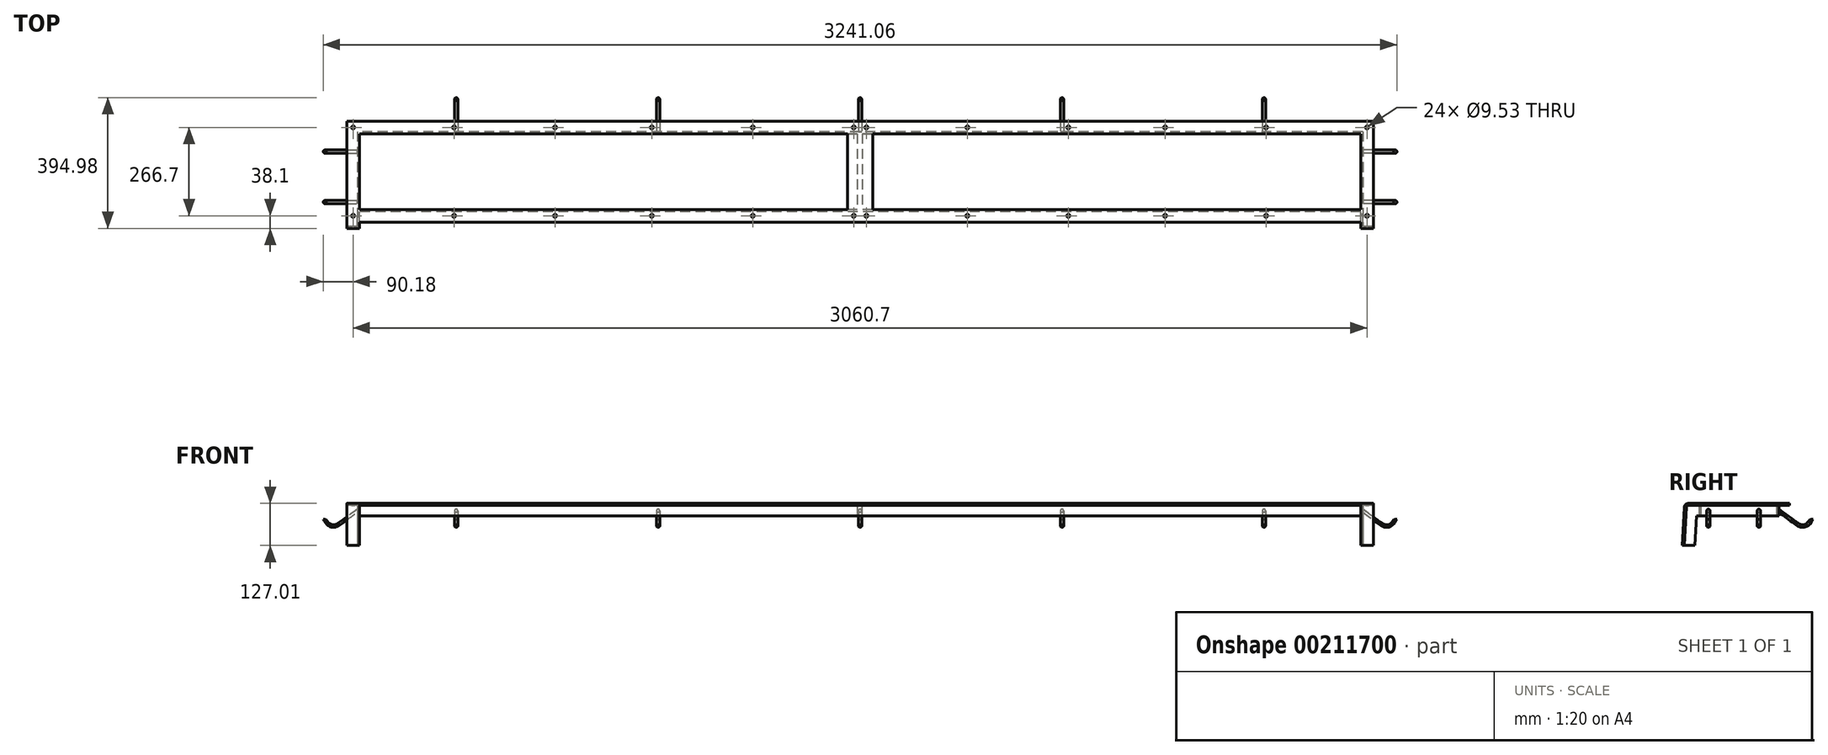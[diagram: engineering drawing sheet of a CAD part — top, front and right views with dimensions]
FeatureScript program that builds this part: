
annotation { "Feature Type Name" : "Feature", "Feature Type Description" : "" }
export const myFeature = defineFeature(function(context is Context, id is Id, definition is map)
    precondition{}
    {
        {
            var Q0;
            Q0=qCreatedBy(makeId("Right.planeOp"),FACE);
            var sketch = newSketch(context, id + "F0", { "sketchPlane" : qUnion([Q0])});
            skLineSegment(sketch, "E0", {"start": v(304.8, 0) * mm, "end": v(0, 0) * mm, "construction": true});
            skArc(sketch, "E1", {"start": v(0, 0) * mm, "mid": v(-6.55, -2.6) * mm, "end": v(-9.51, -9) * mm, "construction": true});
            skLineSegment(sketch, "E2", {"start": v(-9.51, -9) * mm, "end": v(-15.87, -123.83) * mm, "construction": true});
            skLineSegment(sketch, "E3.0", {"start": v(-12.68, -8.82) * mm, "end": v(-19.05, -123.83) * mm});
            skArc(sketch, "E3.1", {"start": v(0, 3.18) * mm, "mid": v(-8.73, -0.3) * mm, "end": v(-12.68, -8.82) * mm});
            skLineSegment(sketch, "E3.2", {"start": v(304.8, 3.18) * mm, "end": v(0, 3.18) * mm});
            skLineSegment(sketch, "E4", {"start": v(-15.87, -123.83) * mm, "end": v(-19.05, -123.83) * mm});
            skLineSegment(sketch, "E5", {"start": v(304.8, 3.18) * mm, "end": v(304.8, 0) * mm});
            skLineSegment(sketch, "E6.0", {"start": v(-6.34, -9.17) * mm, "end": v(-12.7, -123.83) * mm});
            skArc(sketch, "E6.1", {"start": v(0, -3.17) * mm, "mid": v(-4.36, -4.91) * mm, "end": v(-6.34, -9.17) * mm});
            skLineSegment(sketch, "E6.2", {"start": v(304.8, -3.17) * mm, "end": v(0, -3.17) * mm});
            skLineSegment(sketch, "E7", {"start": v(-15.87, -123.83) * mm, "end": v(-12.7, -123.83) * mm});
            skLineSegment(sketch, "E8", {"start": v(304.8, -3.17) * mm, "end": v(304.8, 0) * mm});
            skLineSegment(sketch, "E9", {"start": v(273.05, 0) * mm, "end": v(273.05, -34.92) * mm});
            skLineSegment(sketch, "E10", {"start": v(-12.7, -123.83) * mm, "end": v(19.1, -123.83) * mm});
            skLineSegment(sketch, "E11.0", {"start": v(24.03, -34.92) * mm, "end": v(19.1, -123.83) * mm});
            skLineSegment(sketch, "E11.1", {"start": v(273.05, -34.92) * mm, "end": v(24.03, -34.92) * mm});
            skSolve(sketch);
        }
        {
            var Q0;
            Q0=makeQuery(id+"F0.imprint","IMPRINT",FACE,{"disambiguationData":[TD([[makeQuery(id+"F0.imprint","IMPRINT",EDGE,{"derivedFrom":sQuery(id+"F0.wireOp",EDGE,"E3.0")}),1.0]])]});
            extrude(context, id + "F1", {"entities" : qUnion([Q0]), "depth" : 1549.4 * mm, "hasSecondDirection" : true, "secondDirectionOppositeDirection" : true, "secondDirectionDepth" : 1549.4 * mm});
        }
        {
            var Q0;
            Q0=makeQuery(id+"F0.imprint","IMPRINT",FACE,{"disambiguationData":[TD([[makeQuery(id+"F0.imprint","IMPRINT",EDGE,{"derivedFrom":sQuery(id+"F0.wireOp",EDGE,"E6.0")}),1.0]])]});
            extrude(context, id + "F2", {"entities" : qUnion([Q0]), "operationType" : NewBodyOperationType.ADD, "depth" : 1517.65 * mm, "hasSecondDirection" : true, "secondDirectionOppositeDirection" : true, "secondDirectionDepth" : 1517.65 * mm});
        }
        {
            var Q0;
            Q0=makeQuery(id+"F1.opExtrude","SWEPT_FACE",FACE,{"disambiguationData":[OSD([sQuery(id+"F0.wireOp",EDGE,"E3.2")])]});
            var sketch = newSketch(context, id + "F3", { "sketchPlane" : qUnion([Q0])});
            skLineSegment(sketch, "E12.bottom", {"start": v(1511.3, 266.7) * mm, "end": v(-1511.3, 266.7) * mm});
            skLineSegment(sketch, "E12.top", {"start": v(1511.3, -266.7) * mm, "end": v(-1511.3, -266.7) * mm});
            skLineSegment(sketch, "E12.left", {"start": v(1511.3, 266.7) * mm, "end": v(1511.3, -266.7) * mm});
            skLineSegment(sketch, "E12.right", {"start": v(-1511.3, 266.7) * mm, "end": v(-1511.3, -266.7) * mm});
            skPoint(sketch, "E12.middle", {"position": v(0, 0) * mm});
            skSolve(sketch);
        }
        {
            var Q0;
            Q0 = qSketchRegion(id + "F3", true);
            extrude(context, id + "F4", {"entities" : qUnion([Q0]), "operationType" : NewBodyOperationType.REMOVE, "endBound" : BoundingType.THROUGH_ALL, "oppositeDirection" : true, "depth" : 25.4 * mm});
        }
        {
            var Q0;
            Q0=qCreatedBy(makeId("Right.planeOp"),FACE);
            var sketch = newSketch(context, id + "F5", { "sketchPlane" : qUnion([Q0])});
            skLineSegment(sketch, "E13.0", {"start": v(304.8, 3.18) * mm, "end": v(0, 3.18) * mm, "construction": true});
            skPoint(sketch, "E14.0", {"position": v(266.7, 3.18) * mm});
            skLineSegment(sketch, "E15", {"start": v(0, 3.18) * mm, "end": v(38.1, 3.18) * mm});
            skLineSegment(sketch, "E16.0", {"start": v(273.05, -34.92) * mm, "end": v(24.03, -34.92) * mm, "construction": true});
            skLineSegment(sketch, "E17", {"start": v(38.1, 3.18) * mm, "end": v(38.1, -34.92) * mm});
            skLineSegment(sketch, "E18", {"start": v(38.1, -34.93) * mm, "end": v(31.75, -34.93) * mm});
            skLineSegment(sketch, "E19", {"start": v(31.75, -34.92) * mm, "end": v(31.75, -3.17) * mm});
            skLineSegment(sketch, "E20", {"start": v(31.75, -3.17) * mm, "end": v(0, -3.17) * mm});
            skLineSegment(sketch, "E21", {"start": v(0, 3.18) * mm, "end": v(0, -3.17) * mm});
            skPoint(sketch, "E22.0", {"position": v(0, 3.18) * mm});
            skSolve(sketch);
        }
        {
            var Q0;
            Q0=makeQuery(id+"F5.imprint","IMPRINT",FACE,{"disambiguationData":[TD([[makeQuery(id+"F5.imprint","IMPRINT",EDGE,{"derivedFrom":sQuery(id+"F5.wireOp",EDGE,"E15")}),-1.0]])]});
            var Q1;
            Q1=makeQuery(id+"F1.opExtrude","SWEPT_BODY",BODY,{"disambiguationData":[OSD([sQuery(id+"F0.wireOp",EDGE,"E3.0"),sQuery(id+"F0.wireOp",EDGE,"E3.1"),sQuery(id+"F0.wireOp",EDGE,"E3.2"),sQuery(id+"F0.wireOp",EDGE,"E4"),sQuery(id+"F0.wireOp",EDGE,"E5"),sQuery(id+"F0.wireOp",EDGE,"E6.0"),sQuery(id+"F0.wireOp",EDGE,"E6.1"),sQuery(id+"F0.wireOp",EDGE,"E6.2"),sQuery(id+"F0.wireOp",EDGE,"E7"),sQuery(id+"F0.wireOp",EDGE,"E8")])]});
            var Q2;
            Q2=makeQuery(id+"F1.opExtrude","SWEPT_BODY",BODY,{"disambiguationData":[OSD([sQuery(id+"F0.wireOp",EDGE,"E3.0"),sQuery(id+"F0.wireOp",EDGE,"E3.1"),sQuery(id+"F0.wireOp",EDGE,"E3.2"),sQuery(id+"F0.wireOp",EDGE,"E4"),sQuery(id+"F0.wireOp",EDGE,"E5"),sQuery(id+"F0.wireOp",EDGE,"E6.0"),sQuery(id+"F0.wireOp",EDGE,"E6.1"),sQuery(id+"F0.wireOp",EDGE,"E6.2"),sQuery(id+"F0.wireOp",EDGE,"E7"),sQuery(id+"F0.wireOp",EDGE,"E8")])]});
            extrude(context, id + "F6", {"entities" : qUnion([Q0]), "operationType" : NewBodyOperationType.ADD, "endBound" : BoundingType.UP_TO_BODY, "endBoundEntityBody" : qUnion([Q1]), "depth" : 25.4 * mm, "hasSecondDirection" : true, "secondDirectionBound" : SecondDirectionBoundingType.UP_TO_BODY, "secondDirectionOppositeDirection" : true, "secondDirectionBoundEntityBody" : qUnion([Q2]), "secondDirectionDepth" : 25.4 * mm});
        }
        {
            var Q0;
            Q0=qCreatedBy(makeId("Right.planeOp"),FACE);
            var sketch = newSketch(context, id + "F7", { "sketchPlane" : qUnion([Q0])});
            skPoint(sketch, "E23.0", {"position": v(38.1, 3.18) * mm});
            skLineSegment(sketch, "E24", {"start": v(266.7, 0) * mm, "end": v(38.1, 0) * mm, "construction": true});
            skLineSegment(sketch, "E25.2", {"start": v(266.7, 3.18) * mm, "end": v(38.1, 3.18) * mm});
            skLineSegment(sketch, "E26", {"start": v(266.7, 3.18) * mm, "end": v(266.7, 0) * mm});
            skLineSegment(sketch, "E27.2", {"start": v(266.7, -3.17) * mm, "end": v(38.1, -3.17) * mm});
            skLineSegment(sketch, "E28", {"start": v(266.7, -3.17) * mm, "end": v(266.7, 0) * mm});
            skLineSegment(sketch, "E29", {"start": v(266.7, 0) * mm, "end": v(266.7, -34.92) * mm});
            skLineSegment(sketch, "E30.1", {"start": v(266.7, -34.92) * mm, "end": v(38.1, -34.92) * mm});
            skPoint(sketch, "E31.0", {"position": v(266.7, 3.18) * mm});
            skPoint(sketch, "E32.0", {"position": v(38.1, -34.92) * mm});
            skLineSegment(sketch, "E33", {"start": v(38.1, -34.92) * mm, "end": v(38.1, 3.18) * mm});
            skSolve(sketch);
        }
        {
            var Q0;
            {var subQ3=sQuery(id+"F7.wireOp",EDGE,"E25.2");Q0=makeQuery(id+"F7.imprint","IMPRINT",FACE,{"disambiguationData":[TD([[makeQuery(id+"F7.imprint","IMPRINT",EDGE,{"derivedFrom":subQ3}),1.0]])]});}
            extrude(context, id + "F8", {"entities" : qUnion([Q0]), "operationType" : NewBodyOperationType.ADD, "depth" : 38.1 * mm, "hasSecondDirection" : true, "secondDirectionOppositeDirection" : true, "secondDirectionDepth" : 38.1 * mm});
        }
        {
            var Q0;
            {var subQ0=sQuery(id+"F7.wireOp",EDGE,"E27.2");Q0=makeQuery(id+"F7.imprint","IMPRINT",FACE,{"disambiguationData":[TD([[makeQuery(id+"F7.imprint","IMPRINT",EDGE,{"derivedFrom":subQ0}),1.0]])]});}
            extrude(context, id + "F9", {"entities" : qUnion([Q0]), "operationType" : NewBodyOperationType.ADD, "depth" : 6.35 * mm, "hasSecondDirection" : true, "secondDirectionOppositeDirection" : true, "secondDirectionDepth" : 8.9 * mm});
        }
        {
            var Q0;
            Q0=makeQuery(id+"F8.boolean.opBoolean","MERGE",FACE,{"derivedFrom":[makeQuery(id+"F6.boolean.opBoolean","MERGE",FACE,{"derivedFrom":[makeQuery(id+"F1.opExtrude","SWEPT_FACE",FACE,{"disambiguationData":[OSD([sQuery(id+"F0.wireOp",EDGE,"E3.2")])]}),makeQuery(id+"F6.opExtrude","SWEPT_FACE",FACE,{"disambiguationData":[OSD([sQuery(id+"F5.wireOp",EDGE,"E15")])]})]}),makeQuery(id+"F8.opExtrude","SWEPT_FACE",FACE,{"disambiguationData":[OSD([sQuery(id+"F7.wireOp",EDGE,"E25.2")])]})]});
            var sketch = newSketch(context, id + "F10", { "sketchPlane" : qUnion([Q0])});
            skPoint(sketch, "E34", {"position": v(-1530.35, 285.75) * mm});
            skPoint(sketch, "E35", {"position": v(-19.05, 285.75) * mm});
            skPoint(sketch, "E36", {"position": v(-628.65, 285.75) * mm});
            skPoint(sketch, "E37", {"position": v(-920.75, 285.75) * mm});
            skPoint(sketch, "E38", {"position": v(-1225.55, 285.75) * mm});
            skPoint(sketch, "E39", {"position": v(-323.85, 285.75) * mm});
            skLineSegment(sketch, "E40", {"start": v(-1319.31, 152.4) * mm, "end": v(-616.3, 152.4) * mm, "construction": true});
            skPoint(sketch, "E41.MirrorP", {"position": v(-19.05, 19.05) * mm});
            skPoint(sketch, "E42.MirrorP", {"position": v(-323.85, 19.05) * mm});
            skPoint(sketch, "E43.MirrorP", {"position": v(-628.65, 19.05) * mm});
            skPoint(sketch, "E44.MirrorP", {"position": v(-920.75, 19.05) * mm});
            skPoint(sketch, "E45.MirrorP", {"position": v(-1225.55, 19.05) * mm});
            skPoint(sketch, "E46.MirrorP", {"position": v(-1530.35, 19.05) * mm});
            skPoint(sketch, "E47.MirrorP", {"position": v(1530.35, 285.75) * mm});
            skPoint(sketch, "E48.MirrorP", {"position": v(1530.35, 19.05) * mm});
            skPoint(sketch, "E49.MirrorP", {"position": v(1225.55, 19.05) * mm});
            skPoint(sketch, "E50.MirrorP", {"position": v(1225.55, 285.75) * mm});
            skPoint(sketch, "E51.MirrorP", {"position": v(920.75, 285.75) * mm});
            skPoint(sketch, "E52.MirrorP", {"position": v(920.75, 19.05) * mm});
            skPoint(sketch, "E53.MirrorP", {"position": v(628.65, 285.75) * mm});
            skPoint(sketch, "E54.MirrorP", {"position": v(628.65, 19.05) * mm});
            skPoint(sketch, "E55.MirrorP", {"position": v(323.85, 285.75) * mm});
            skPoint(sketch, "E56.MirrorP", {"position": v(323.85, 19.05) * mm});
            skPoint(sketch, "E57.MirrorP", {"position": v(19.05, 19.05) * mm});
            skPoint(sketch, "E58.MirrorP", {"position": v(19.05, 285.75) * mm});
            skSolve(sketch);
        }
        {
            var Q0;
            Q0=sQuery(id+"F10.wireOp",VERTEX,"E48.MirrorP");
            var Q1;
            Q1=sQuery(id+"F10.wireOp",VERTEX,"E47.MirrorP");
            var Q2;
            Q2=sQuery(id+"F10.wireOp",VERTEX,"E50.MirrorP");
            var Q3;
            Q3=sQuery(id+"F10.wireOp",VERTEX,"E49.MirrorP");
            var Q4;
            Q4=sQuery(id+"F10.wireOp",VERTEX,"E51.MirrorP");
            var Q5;
            Q5=sQuery(id+"F10.wireOp",VERTEX,"E53.MirrorP");
            var Q6;
            Q6=sQuery(id+"F10.wireOp",VERTEX,"E52.MirrorP");
            var Q7;
            Q7=sQuery(id+"F10.wireOp",VERTEX,"E54.MirrorP");
            var Q8;
            Q8=sQuery(id+"F10.wireOp",VERTEX,"E56.MirrorP");
            var Q9;
            Q9=sQuery(id+"F10.wireOp",VERTEX,"E55.MirrorP");
            var Q10;
            Q10=sQuery(id+"F10.wireOp",VERTEX,"E35");
            var Q11;
            Q11=sQuery(id+"F10.wireOp",VERTEX,"E57.MirrorP");
            var Q12;
            Q12=sQuery(id+"F10.wireOp",VERTEX,"E58.MirrorP");
            var Q13;
            Q13=sQuery(id+"F10.wireOp",VERTEX,"E41.MirrorP");
            var Q14;
            Q14=sQuery(id+"F10.wireOp",VERTEX,"E42.MirrorP");
            var Q15;
            Q15=sQuery(id+"F10.wireOp",VERTEX,"E39");
            var Q16;
            Q16=sQuery(id+"F10.wireOp",VERTEX,"E36");
            var Q17;
            Q17=sQuery(id+"F10.wireOp",VERTEX,"E43.MirrorP");
            var Q18;
            Q18=sQuery(id+"F10.wireOp",VERTEX,"E44.MirrorP");
            var Q19;
            Q19=sQuery(id+"F10.wireOp",VERTEX,"E37");
            var Q20;
            Q20=sQuery(id+"F10.wireOp",VERTEX,"E38");
            var Q21;
            Q21=sQuery(id+"F10.wireOp",VERTEX,"E45.MirrorP");
            var Q22;
            Q22=sQuery(id+"F10.wireOp",VERTEX,"E34");
            var Q23;
            Q23=sQuery(id+"F10.wireOp",VERTEX,"E46.MirrorP");
            var Q24;
            Q24=makeQuery(id+"F1.opExtrude","SWEPT_BODY",BODY,{"disambiguationData":[OSD([sQuery(id+"F0.wireOp",EDGE,"E3.0"),sQuery(id+"F0.wireOp",EDGE,"E3.1"),sQuery(id+"F0.wireOp",EDGE,"E3.2"),sQuery(id+"F0.wireOp",EDGE,"E4"),sQuery(id+"F0.wireOp",EDGE,"E5"),sQuery(id+"F0.wireOp",EDGE,"E6.0"),sQuery(id+"F0.wireOp",EDGE,"E6.1"),sQuery(id+"F0.wireOp",EDGE,"E6.2"),sQuery(id+"F0.wireOp",EDGE,"E7"),sQuery(id+"F0.wireOp",EDGE,"E8")])]});
            hole(context, id + "F11", {"style" : HoleStyle.SIMPLE, "endStyle" : HoleEndStyle.BLIND, "holeDiameter" : 9.52 * mm, "holeDepth" : 12.7 * mm, "startFromSketch" : true, "locations" : qUnion([Q0, Q1, Q2, Q3, Q4, Q5, Q6, Q7, Q8, Q9, Q10, Q11, Q12, Q13, Q14, Q15, Q16, Q17, Q18, Q19, Q20, Q21, Q22, Q23]), "scope" : qUnion([Q24])});
        }
        {
            var Q0;
            Q0=qCreatedBy(makeId("Right.planeOp"),FACE);
            var sketch = newSketch(context, id + "F12", { "sketchPlane" : qUnion([Q0])});
            skPoint(sketch, "E59.0", {"position": v(273.05, -19.05) * mm});
            skFitSpline(sketch, "E60", {"points": [v(273.05, -19.05) * mm, v(342.92, -65.18) * mm, v(371.2, -45.3) * mm], "startDerivative": vector(281.31, -205.32) * mm, "endDerivative": vector(85.1, 152.4) * mm});
            skSolve(sketch);
        }
        {
            var Q0;
            Q0=makeQuery(id+"F2.opExtrude","SWEPT_FACE",FACE,{"disambiguationData":[OSD([sQuery(id+"F0.wireOp",EDGE,"E9")])]});
            var sketch = newSketch(context, id + "F13", { "sketchPlane" : qUnion([Q0])});
            skPoint(sketch, "E61.0", {"position": v(0, -19.05) * mm});
            skCircle(sketch, "E62", {"center": v(0, -19.05) * mm, "radius": 4.76 * mm});
            skSolve(sketch);
        }
        {
            var Q0;
            Q0 = qSketchRegion(id + "F13", true);
            var Q1;
            Q1 = qConstructionFilter(qBodyType(qCreatedBy(id + "F12" ,EDGE), BodyType.WIRE), ConstructionObject.NO);
            sweep(context, id + "F14", {"operationType" : NewBodyOperationType.ADD, "profiles" : qUnion([Q0]), "path" : qUnion([Q1])});
        }
        {
            var Q0;
            Q0=makeQuery(id+"F2.opExtrude","SWEPT_FACE",FACE,{"disambiguationData":[OSD([sQuery(id+"F0.wireOp",EDGE,"E9")])]});
            var sketch = newSketch(context, id + "F15", { "sketchPlane" : qUnion([Q0])});
            skPoint(sketch, "E63", {"position": v(0, -19.05) * mm});
            skPoint(sketch, "E64", {"position": v(609.6, -19.05) * mm});
            skPoint(sketch, "E65", {"position": v(-609.6, -19.05) * mm});
            skPoint(sketch, "E66", {"position": v(1219.2, -19.05) * mm});
            skPoint(sketch, "E67", {"position": v(-1219.2, -19.05) * mm});
            skSolve(sketch);
        }
        {
            var Q0;
            Q0=qCreatedBy(makeId("Right.planeOp"),FACE);
            cPlane(context, id + "F16", {"entities" : qUnion([Q0]), "cplaneType" : CPlaneType.OFFSET, "offset" : 1219.2 * mm, "width" : 152.4 * mm, "height" : 152.4 * mm});
        }
        {
            var Q0;
            Q0=qCreatedBy(makeId("Right.planeOp"),FACE);
            cPlane(context, id + "F17", {"entities" : qUnion([Q0]), "cplaneType" : CPlaneType.OFFSET, "offset" : 609.6 * mm, "width" : 152.4 * mm, "height" : 152.4 * mm});
        }
        {
            var Q0;
            Q0=qCreatedBy(makeId("Right.planeOp"),FACE);
            cPlane(context, id + "F18", {"entities" : qUnion([Q0]), "cplaneType" : CPlaneType.OFFSET, "offset" : 609.6 * mm, "oppositeDirection" : true, "width" : 152.4 * mm, "height" : 152.4 * mm});
        }
        {
            var Q0;
            Q0=qCreatedBy(makeId("Right.planeOp"),FACE);
            cPlane(context, id + "F19", {"entities" : qUnion([Q0]), "cplaneType" : CPlaneType.OFFSET, "offset" : 1219.2 * mm, "oppositeDirection" : true, "width" : 152.4 * mm, "height" : 152.4 * mm});
        }
        {
            var Q0;
            Q0=qCreatedBy(id+"F16.planeOp",FACE);
            var sketch = newSketch(context, id + "F20", { "sketchPlane" : qUnion([Q0])});
            skPoint(sketch, "E68.0", {"position": v(273.05, -19.05) * mm});
            skFitSpline(sketch, "E69", {"points": [v(273.05, -19.05) * mm, v(342.92, -65.18) * mm, v(371.2, -45.3) * mm], "startDerivative": vector(281.31, -205.32) * mm, "endDerivative": vector(85.1, 152.4) * mm});
            skSolve(sketch);
        }
        {
            var Q0;
            Q0=qCreatedBy(id+"F17.planeOp",FACE);
            var sketch = newSketch(context, id + "F21", { "sketchPlane" : qUnion([Q0])});
            skPoint(sketch, "E70.0", {"position": v(273.05, -19.05) * mm});
            skFitSpline(sketch, "E71", {"points": [v(273.05, -19.05) * mm, v(342.92, -65.18) * mm, v(371.2, -45.3) * mm], "startDerivative": vector(281.31, -205.32) * mm, "endDerivative": vector(85.1, 152.4) * mm});
            skSolve(sketch);
        }
        {
            var Q0;
            Q0=qCreatedBy(id+"F18.planeOp",FACE);
            var sketch = newSketch(context, id + "F22", { "sketchPlane" : qUnion([Q0])});
            skPoint(sketch, "E72.0", {"position": v(273.05, -19.05) * mm});
            skFitSpline(sketch, "E73", {"points": [v(273.05, -19.05) * mm, v(342.92, -65.18) * mm, v(371.2, -45.3) * mm], "startDerivative": vector(281.31, -205.32) * mm, "endDerivative": vector(85.1, 152.4) * mm});
            skSolve(sketch);
        }
        {
            var Q0;
            Q0=qCreatedBy(id+"F19.planeOp",FACE);
            var sketch = newSketch(context, id + "F23", { "sketchPlane" : qUnion([Q0])});
            skPoint(sketch, "E74.0", {"position": v(273.05, -19.05) * mm});
            skFitSpline(sketch, "E75", {"points": [v(273.05, -19.05) * mm, v(342.92, -65.18) * mm, v(371.2, -45.3) * mm], "startDerivative": vector(281.31, -205.32) * mm, "endDerivative": vector(85.1, 152.4) * mm});
            skSolve(sketch);
        }
        {
            var Q0;
            {var subQ0=sQuery(id+"F0.wireOp",EDGE,"E9");Q0=makeQuery(id+"F15.imprint","IMPRINT",FACE,{"disambiguationData":[TD([[makeQuery(id+"F15.imprint","IMPRINT",EDGE,{"derivedFrom":makeQuery(id+"F2.opExtrude","CAP_EDGE",EDGE,{"disambiguationData":[OSD([subQ0])],"isStart":true})}),-1.0]])]});}
            var sketch = newSketch(context, id + "F24", { "sketchPlane" : qUnion([Q0])});
            skPoint(sketch, "E76.0", {"position": v(-1219.2, -19.05) * mm});
            skCircle(sketch, "E77", {"center": v(-1219.2, -19.05) * mm, "radius": 4.76 * mm});
            skSolve(sketch);
        }
        {
            var Q0;
            {var subQ0=sQuery(id+"F0.wireOp",EDGE,"E9");Q0=makeQuery(id+"F15.imprint","IMPRINT",FACE,{"disambiguationData":[TD([[makeQuery(id+"F15.imprint","IMPRINT",EDGE,{"derivedFrom":makeQuery(id+"F2.opExtrude","CAP_EDGE",EDGE,{"disambiguationData":[OSD([subQ0])],"isStart":true})}),-1.0]])]});}
            var sketch = newSketch(context, id + "F25", { "sketchPlane" : qUnion([Q0])});
            skPoint(sketch, "E78.0", {"position": v(-609.6, -19.05) * mm});
            skCircle(sketch, "E79", {"center": v(-609.6, -19.05) * mm, "radius": 4.76 * mm});
            skSolve(sketch);
        }
        {
            var Q0;
            {var subQ0=sQuery(id+"F0.wireOp",EDGE,"E9");Q0=makeQuery(id+"F15.imprint","IMPRINT",FACE,{"disambiguationData":[TD([[makeQuery(id+"F15.imprint","IMPRINT",EDGE,{"derivedFrom":makeQuery(id+"F2.opExtrude","CAP_EDGE",EDGE,{"disambiguationData":[OSD([subQ0])],"isStart":true})}),-1.0]])]});}
            var sketch = newSketch(context, id + "F26", { "sketchPlane" : qUnion([Q0])});
            skPoint(sketch, "E80.0", {"position": v(609.6, -19.05) * mm});
            skCircle(sketch, "E81", {"center": v(609.6, -19.05) * mm, "radius": 4.76 * mm});
            skSolve(sketch);
        }
        {
            var Q0;
            {var subQ0=sQuery(id+"F0.wireOp",EDGE,"E9");Q0=makeQuery(id+"F15.imprint","IMPRINT",FACE,{"disambiguationData":[TD([[makeQuery(id+"F15.imprint","IMPRINT",EDGE,{"derivedFrom":makeQuery(id+"F2.opExtrude","CAP_EDGE",EDGE,{"disambiguationData":[OSD([subQ0])],"isStart":true})}),-1.0]])]});}
            var sketch = newSketch(context, id + "F27", { "sketchPlane" : qUnion([Q0])});
            skPoint(sketch, "E82.0", {"position": v(1219.2, -19.05) * mm});
            skCircle(sketch, "E83", {"center": v(1219.2, -19.05) * mm, "radius": 4.76 * mm});
            skSolve(sketch);
        }
        {
            var Q0;
            Q0 = qSketchRegion(id + "F24", true);
            var Q1;
            Q1 = qConstructionFilter(qBodyType(qCreatedBy(id + "F20" ,EDGE), BodyType.WIRE), ConstructionObject.NO);
            sweep(context, id + "F28", {"operationType" : NewBodyOperationType.ADD, "profiles" : qUnion([Q0]), "path" : qUnion([Q1])});
        }
        {
            var Q0;
            Q0 = qSketchRegion(id + "F25", true);
            var Q1;
            Q1 = qConstructionFilter(qBodyType(qCreatedBy(id + "F21" ,EDGE), BodyType.WIRE), ConstructionObject.NO);
            sweep(context, id + "F29", {"operationType" : NewBodyOperationType.ADD, "profiles" : qUnion([Q0]), "path" : qUnion([Q1])});
        }
        {
            var Q0;
            Q0 = qSketchRegion(id + "F26", true);
            var Q1;
            Q1 = qConstructionFilter(qBodyType(qCreatedBy(id + "F22" ,EDGE), BodyType.WIRE), ConstructionObject.NO);
            sweep(context, id + "F30", {"operationType" : NewBodyOperationType.ADD, "profiles" : qUnion([Q0]), "path" : qUnion([Q1])});
        }
        {
            var Q0;
            Q0 = qSketchRegion(id + "F27", true);
            var Q1;
            Q1 = qConstructionFilter(qBodyType(qCreatedBy(id + "F23" ,EDGE), BodyType.WIRE), ConstructionObject.NO);
            sweep(context, id + "F31", {"operationType" : NewBodyOperationType.ADD, "profiles" : qUnion([Q0]), "path" : qUnion([Q1])});
        }
        {
            var Q0;
            Q0=makeQuery(id+"F2.opExtrude","CAP_FACE",FACE,{"disambiguationData":[OSD([sQuery(id+"F0.wireOp",EDGE,"E6.0"),sQuery(id+"F0.wireOp",EDGE,"E6.1"),sQuery(id+"F0.wireOp",EDGE,"E6.2"),sQuery(id+"F0.wireOp",EDGE,"E9"),sQuery(id+"F0.wireOp",EDGE,"E10"),sQuery(id+"F0.wireOp",EDGE,"E11.0"),sQuery(id+"F0.wireOp",EDGE,"E11.1")])],"isStart":false});
            var sketch = newSketch(context, id + "F32", { "sketchPlane" : qUnion([Q0])});
            skPoint(sketch, "E84", {"position": v(212.72, -19.05) * mm});
            skPoint(sketch, "E84.positionSnap0", {"position": v(273.05, -19.05) * mm});
            skPoint(sketch, "E85", {"position": v(60.32, -19.05) * mm});
            skSolve(sketch);
        }
        {
            var Q0;
            Q0=makeQuery(id+"F32.imprint","IMPRINT",FACE,{"disambiguationData":[TD([[makeQuery(id+"F32.imprint","IMPRINT",EDGE,{"derivedFrom":makeQuery(id+"F2.opExtrude","CAP_EDGE",EDGE,{"disambiguationData":[OSD([sQuery(id+"F0.wireOp",EDGE,"E9")])],"isStart":false})}),-1.0]])]});
            var sketch = newSketch(context, id + "F33", { "sketchPlane" : qUnion([Q0])});
            skPoint(sketch, "E86.0", {"position": v(60.32, -19.05) * mm});
            skCircle(sketch, "E87", {"center": v(60.32, -19.05) * mm, "radius": 4.76 * mm});
            skSolve(sketch);
        }
        {
            var Q0;
            Q0=makeQuery(id+"F32.imprint","IMPRINT",FACE,{"disambiguationData":[TD([[makeQuery(id+"F32.imprint","IMPRINT",EDGE,{"derivedFrom":makeQuery(id+"F2.opExtrude","CAP_EDGE",EDGE,{"disambiguationData":[OSD([sQuery(id+"F0.wireOp",EDGE,"E9")])],"isStart":false})}),-1.0]])]});
            var sketch = newSketch(context, id + "F34", { "sketchPlane" : qUnion([Q0])});
            skPoint(sketch, "E88.0", {"position": v(212.72, -19.05) * mm});
            skCircle(sketch, "E89", {"center": v(212.72, -19.05) * mm, "radius": 4.76 * mm});
            skSolve(sketch);
        }
        {
            var Q0;
            Q0=makeQuery(id+"F2.opExtrude","CAP_FACE",FACE,{"disambiguationData":[OSD([sQuery(id+"F0.wireOp",EDGE,"E6.0"),sQuery(id+"F0.wireOp",EDGE,"E6.1"),sQuery(id+"F0.wireOp",EDGE,"E6.2"),sQuery(id+"F0.wireOp",EDGE,"E9"),sQuery(id+"F0.wireOp",EDGE,"E10"),sQuery(id+"F0.wireOp",EDGE,"E11.0"),sQuery(id+"F0.wireOp",EDGE,"E11.1")])],"isStart":true});
            var sketch = newSketch(context, id + "F35", { "sketchPlane" : qUnion([Q0])});
            skPoint(sketch, "E90.0", {"position": v(-212.72, -19.05) * mm});
            skPoint(sketch, "E91.0", {"position": v(-60.32, -19.05) * mm});
            skCircle(sketch, "E92", {"center": v(-212.72, -19.05) * mm, "radius": 4.76 * mm});
            skSolve(sketch);
        }
        {
            var Q0;
            Q0=makeQuery(id+"F35.imprint","IMPRINT",FACE,{"disambiguationData":[TD([[makeQuery(id+"F35.imprint","IMPRINT",EDGE,{"derivedFrom":sQuery(id+"F35.wireOp",EDGE,"E92")}),-1.0]])]});
            var sketch = newSketch(context, id + "F36", { "sketchPlane" : qUnion([Q0])});
            skPoint(sketch, "E93.0", {"position": v(-60.32, -19.05) * mm});
            skCircle(sketch, "E94", {"center": v(-60.32, -19.05) * mm, "radius": 4.76 * mm});
            skSolve(sketch);
        }
        {
            var Q0;
            Q0=qCreatedBy(makeId("Front.planeOp"),FACE);
            cPlane(context, id + "F37", {"entities" : qUnion([Q0]), "cplaneType" : CPlaneType.OFFSET, "offset" : 60.32 * mm, "oppositeDirection" : true, "width" : 152.4 * mm, "height" : 152.4 * mm});
        }
        {
            var Q0;
            Q0=qCreatedBy(makeId("Front.planeOp"),FACE);
            cPlane(context, id + "F38", {"entities" : qUnion([Q0]), "cplaneType" : CPlaneType.OFFSET, "offset" : 212.72 * mm, "oppositeDirection" : true, "width" : 152.4 * mm, "height" : 152.4 * mm});
        }
        {
            var Q0;
            Q0=qCreatedBy(id+"F37.planeOp",FACE);
            var sketch = newSketch(context, id + "F39", { "sketchPlane" : qUnion([Q0])});
            skPoint(sketch, "E95.0", {"position": v(1517.65, -19.05) * mm});
            skFitSpline(sketch, "E96", {"points": [v(1517.65, -19.05) * mm, v(1587.52, -65.18) * mm, v(1615.8, -45.3) * mm], "startDerivative": vector(281.31, -205.32) * mm, "endDerivative": vector(85.1, 152.4) * mm});
            skSolve(sketch);
        }
        {
            var Q0;
            Q0=qCreatedBy(id+"F38.planeOp",FACE);
            var sketch = newSketch(context, id + "F40", { "sketchPlane" : qUnion([Q0])});
            skPoint(sketch, "E97.0", {"position": v(1517.65, -19.05) * mm});
            skFitSpline(sketch, "E98", {"points": [v(1517.65, -19.05) * mm, v(1587.52, -65.18) * mm, v(1615.8, -45.3) * mm], "startDerivative": vector(281.31, -205.32) * mm, "endDerivative": vector(85.1, 152.4) * mm});
            skSolve(sketch);
        }
        {
            var Q0;
            Q0=qCreatedBy(id+"F37.planeOp",FACE);
            var sketch = newSketch(context, id + "F41", { "sketchPlane" : qUnion([Q0])});
            skPoint(sketch, "E99.0", {"position": v(-1517.65, -19.05) * mm});
            skFitSpline(sketch, "E100.MirrorCS", {"points": [v(-1517.65, -19.05) * mm, v(-1587.52, -65.18) * mm, v(-1615.8, -45.3) * mm], "startDerivative": vector(-281.31, -205.32) * mm, "endDerivative": vector(-85.1, 152.4) * mm});
            skSolve(sketch);
        }
        {
            var Q0;
            Q0=qCreatedBy(id+"F38.planeOp",FACE);
            var sketch = newSketch(context, id + "F42", { "sketchPlane" : qUnion([Q0])});
            skPoint(sketch, "E101.0", {"position": v(-1517.65, -19.05) * mm});
            skFitSpline(sketch, "E102.MirrorCS", {"points": [v(-1517.65, -19.05) * mm, v(-1587.52, -65.18) * mm, v(-1615.8, -45.3) * mm], "startDerivative": vector(-281.31, -205.32) * mm, "endDerivative": vector(-85.1, 152.4) * mm});
            skSolve(sketch);
        }
        {
            var Q0;
            Q0 = qSketchRegion(id + "F33", true);
            var Q1;
            Q1 = qConstructionFilter(qBodyType(qCreatedBy(id + "F39" ,EDGE), BodyType.WIRE), ConstructionObject.NO);
            sweep(context, id + "F43", {"operationType" : NewBodyOperationType.ADD, "profiles" : qUnion([Q0]), "path" : qUnion([Q1])});
        }
        {
            var Q0;
            Q0 = qSketchRegion(id + "F34", true);
            var Q1;
            Q1 = qConstructionFilter(qBodyType(qCreatedBy(id + "F40" ,EDGE), BodyType.WIRE), ConstructionObject.NO);
            sweep(context, id + "F44", {"operationType" : NewBodyOperationType.ADD, "profiles" : qUnion([Q0]), "path" : qUnion([Q1])});
        }
        {
            var Q0;
            Q0 = qSketchRegion(id + "F35", true);
            var Q1;
            Q1 = qConstructionFilter(qBodyType(qCreatedBy(id + "F42" ,EDGE), BodyType.WIRE), ConstructionObject.NO);
            sweep(context, id + "F45", {"operationType" : NewBodyOperationType.ADD, "profiles" : qUnion([Q0]), "path" : qUnion([Q1])});
        }
        {
            var Q0;
            Q0 = qSketchRegion(id + "F36", true);
            var Q1;
            Q1 = qConstructionFilter(qBodyType(qCreatedBy(id + "F41" ,EDGE), BodyType.WIRE), ConstructionObject.NO);
            sweep(context, id + "F46", {"operationType" : NewBodyOperationType.ADD, "profiles" : qUnion([Q0]), "path" : qUnion([Q1])});
        }
    });
